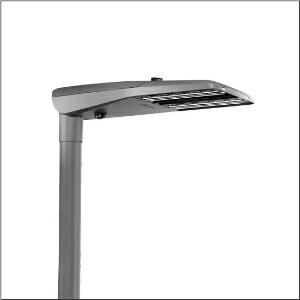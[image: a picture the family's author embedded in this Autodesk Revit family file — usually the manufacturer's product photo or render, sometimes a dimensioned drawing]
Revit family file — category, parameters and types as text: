
# Revit family: streetlight_sl_11_iq_midi___st1_2a_5xc3a21y08me_d9a7
name_source: partatom
category: Lighting Fixtures
units: mm (PartAtom-declared; Revit-internal decimal feet)

## family parameters
Cut with Voids When Loaded = No
Host = Face
Light Source = No
Part Type = Normal
Room Calculation Point = No
Round Connector Dimension = Use Diameter
Shared = No

## types (1)
- --- (1 x LED, 14840 lm, 122.8 W, 2200K)
    Apparent Load = 123 VA
    CIE Flux Codes = 32 70 96 100 100
    Color Rendering = 70
    Color Temperature = 2200K
    Default Elevation = 1800 mm
    Description = Streetlight SL 11 iQ midi, mast luminaire, primary light control with 3 zone facetted reflector, of plastic, silver coated, highly specular, primary optical cover: cover, of PMMA, transparent, light distribution: ST1.2a, light emission: direct distribution, primary light characteristic: asymmetric, installation type: post-top, side-entry, LED, High Power LED, rated luminous flux: 14.840lm, luminous efficacy: 121lm/W, light colour: 722, colour temperature: 2200K, control: presetting dimming logarithmic, Street-Remote, Auto-Match, Temp-Guard, Lumen-Switch, Night-Set, Smart-Wire, Light-Fading, Desk-Remote (wireless, voltage-free reading and setting of iQ features in the workshop via application-optimized NFC function/RFID function), optimised constant luminous flux control (CLO 2.0), with cable H07RN-F 5x 1.5mm², mains connection: 230..240V, AC, 50/60Hz, connection cable pre-assembled, cable length: 12,5m, start of lifetime: 123W, end of service life: 130W, reduction: 56W, luminaire housing, of diecast aluminium, powder-coated, Siteco® metallic grey (DB 702S), please order mast flange separately, inclination adjustable without tools: 0°, 5°, 10°, 15° (post-top) | 0°, -5°, -10°, -15° (side-entry), sealing non-destructively replaceable, multi-level sealing system, length: 780mm, width: 376mm, height: 118mm, mast flange for spigot size: 42mm (side-entry): 5XC10008XM4, 60/48mm (side-entry/post-top): 5XC10108XM2, 76/60mm (side-entry/post-top): 5XC10108XM1, equipment: Power, Smart Interface below and above, protection rating (complete): IP66, insulation class (complete): insulation class II (safety insulation), certification: CE, ENEC, VDE, UKCA, impact resistance: IK09, permissible operating ambient temperature for outdoor applications: -25..+50°C, standard-compliant lighting for roads and squares, Environmental Product Declaration (EPD) tested and certified by an independent institute, packaging unit: 1 piece

Light Distribution: ST1.2a
    Height = 118 mm
    Lamp = 1 x LED
    Lamp Light Flux = 14840 lm
    Lamp Power = 122.8 W
    Lamp count = 1
    Length = 780 mm
    Luminous efficacy = 121 lm/W
    Manufacturer = Siteco
    ModVariant = No
    Model = 5XC3A21Y08ME
    Number of Poles = 1
    OnlyDefault = Yes
    Power Factor = 1
    Product Name = Streetlight SL 11 iQ midi | ST1.2a
    Product group = mast luminaire | pylon top
    ProductGroupID = 6100
    Protection Class = Protection class II
    Protection Degree = IP 66
    RLX_Detail_Level = 1
    RLX_Emergency_Light_Flux = 0 lm
    RLX_Emergency_Type = 0
    RLX_Emergency_Type_DB = No
    RlxData = <blob elided: 69829 chars, md5=217f2764>
    Socket = socket
    Standby Power = 0 W
    System Light Flux = 14840 lm
    System Power = 123 W
    Type Comments = factory setting: luminous flux: 100 % | dim-lin: 254 | 553 mA
    Type Image = l_1004429.jpg
    URL = http://relux.com
    VarID = @adj_079083
    Voltage = 0 V
    Weight = 0.00 kg
    Width = 376 mm

## geometry (parser evidence)
native form markers: Blend x4, Sweep x12
no freeform markers — native parametric forms only
